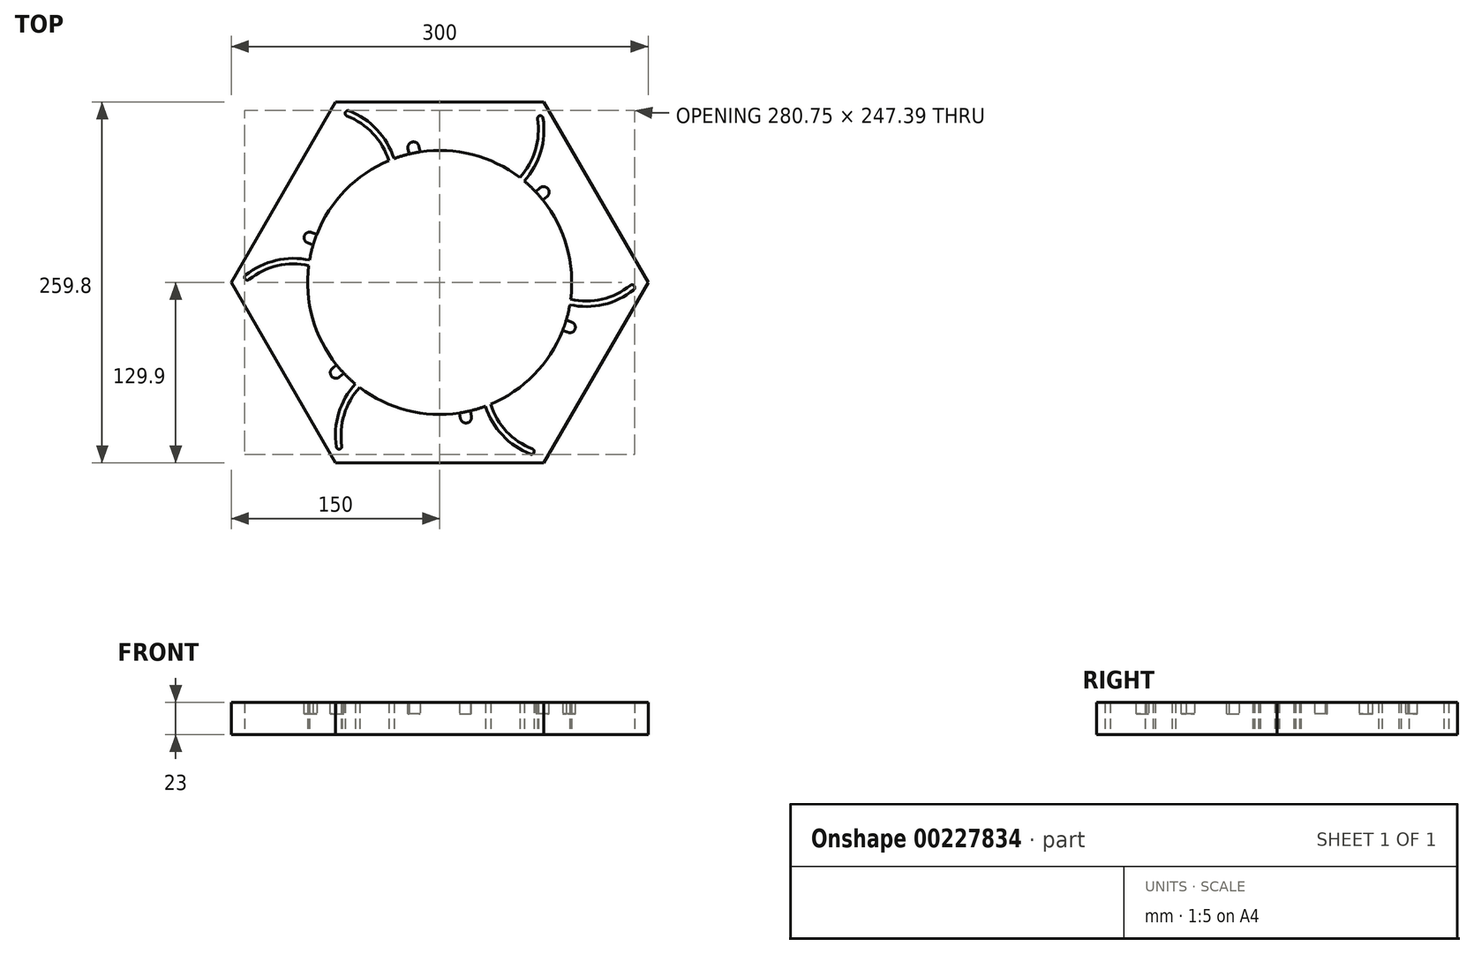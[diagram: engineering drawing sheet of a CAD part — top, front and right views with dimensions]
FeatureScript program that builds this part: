
annotation { "Feature Type Name" : "Feature", "Feature Type Description" : "" }
export const myFeature = defineFeature(function(context is Context, id is Id, definition is map)
    precondition{}
    {
        {
            var Q0;
            Q0=qCreatedBy(makeId("Top.planeOp"),FACE);
            var sketch = newSketch(context, id + "F0", { "sketchPlane" : qUnion([Q0])});
            skCircle(sketch, "E0.cCircle", {"center": v(0, 0) * mm, "radius": 150 * mm, "construction": true});
            skLineSegment(sketch, "E0.0", {"start": v(-75, 129.9) * mm, "end": v(75, 129.9) * mm});
            skLineSegment(sketch, "E0.1", {"start": v(75, 129.9) * mm, "end": v(150, 0) * mm});
            skLineSegment(sketch, "E0.2", {"start": v(150, 0) * mm, "end": v(75, -129.9) * mm});
            skLineSegment(sketch, "E0.3", {"start": v(75, -129.9) * mm, "end": v(-75, -129.9) * mm});
            skLineSegment(sketch, "E0.4", {"start": v(-75, -129.9) * mm, "end": v(-150, 0) * mm});
            skLineSegment(sketch, "E0.5", {"start": v(-150, 0) * mm, "end": v(-75, 129.9) * mm});
            skCircle(sketch, "E1", {"center": v(0, 0) * mm, "radius": 95 * mm});
            skSolve(sketch);
        }
        {
            var Q0;
            Q0=qCreatedBy(makeId("Front.planeOp"),FACE);
            var sketch = newSketch(context, id + "F1", { "sketchPlane" : qUnion([Q0])});
            skLineSegment(sketch, "E2", {"start": v(0, -93.36) * mm, "end": v(0, 93) * mm, "construction": true});
            skSolve(sketch);
        }
        {
            var Q0;
            Q0=makeQuery(id+"F0.imprint","IMPRINT",FACE,{"disambiguationData":[TD([[makeQuery(id+"F0.imprint","IMPRINT",EDGE,{"derivedFrom":sQuery(id+"F0.wireOp",EDGE,"E0.0")}),-1.0]])]});
            extrude(context, id + "F2", {"entities" : qUnion([Q0]), "depth" : 25 * mm, "hasSecondDirection" : true, "secondDirectionOppositeDirection" : false, "secondDirectionDepth" : 2 * mm});
        }
        {
            var Q0;
            Q0=qCreatedBy(makeId("Top.planeOp"),FACE);
            var sketch = newSketch(context, id + "F3", { "sketchPlane" : qUnion([Q0])});
            skArc(sketch, "E3.0", {"start": v(-30.7, 79.26) * mm, "mid": v(-41.9, 106.16) * mm, "end": v(-65.27, 123.56) * mm});
            skArc(sketch, "E4.0", {"start": v(-34.54, 77.66) * mm, "mid": v(-44.72, 103.26) * mm, "end": v(-66.72, 119.83) * mm});
            skArc(sketch, "E5.0", {"start": v(-67.73, 122.7) * mm, "mid": v(-67.88, 121.03) * mm, "end": v(-66.72, 119.83) * mm});
            skArc(sketch, "E6.0", {"start": v(-65.27, 123.56) * mm, "mid": v(-66.66, 123.58) * mm, "end": v(-67.73, 122.7) * mm});
            skArc(sketch, "E7.0", {"start": v(-30.7, 79.26) * mm, "mid": v(-32.63, 78.49) * mm, "end": v(-34.54, 77.66) * mm});
            skSolve(sketch);
        }
        {
            var Q0;
            Q0 = qSketchRegion(id + "F3", true);
            extrude(context, id + "F4", {"entities" : qUnion([Q0]), "depth" : 35 * mm, "hasSecondDirection" : true, "secondDirectionOppositeDirection" : true, "secondDirectionDepth" : 10 * mm});
        }
        {
            var Q0;
            Q0=makeQuery(id+"F4.opExtrude","SWEPT_BODY",BODY,{"disambiguationData":[OSD([sQuery(id+"F3.wireOp",EDGE,"E3.0"),sQuery(id+"F3.wireOp",EDGE,"E4.0"),sQuery(id+"F3.wireOp",EDGE,"E5.0"),sQuery(id+"F3.wireOp",EDGE,"E6.0"),sQuery(id+"F3.wireOp",EDGE,"E7.0")])]});
            var Q1;
            Q1=sQuery(id+"F1.wireOp",EDGE,"E2");
            circularPattern(context, id + "F5", {"entities" : qUnion([Q0]), "axis" : qUnion([Q1]), "angle" : 360 * degree, "instanceCount" : 6, "equalSpace" : true});
        }
        {
            var Q0;
            Q0=makeQuery(id+"F4.opExtrude","SWEPT_BODY",BODY,{"disambiguationData":[OSD([sQuery(id+"F3.wireOp",EDGE,"E3.0"),sQuery(id+"F3.wireOp",EDGE,"E4.0"),sQuery(id+"F3.wireOp",EDGE,"E5.0"),sQuery(id+"F3.wireOp",EDGE,"E6.0"),sQuery(id+"F3.wireOp",EDGE,"E7.0")])]});
            var Q1;
            Q1=makeQuery(id+"F5.opPattern","COPY",BODY,{"derivedFrom":makeQuery(id+"F4.opExtrude","SWEPT_BODY",BODY,{"disambiguationData":[OSD([sQuery(id+"F3.wireOp",EDGE,"E3.0"),sQuery(id+"F3.wireOp",EDGE,"E4.0"),sQuery(id+"F3.wireOp",EDGE,"E5.0"),sQuery(id+"F3.wireOp",EDGE,"E6.0"),sQuery(id+"F3.wireOp",EDGE,"E7.0")])]}),"instanceName":"5"});
            var Q2;
            Q2=makeQuery(id+"F5.opPattern","COPY",BODY,{"derivedFrom":makeQuery(id+"F4.opExtrude","SWEPT_BODY",BODY,{"disambiguationData":[OSD([sQuery(id+"F3.wireOp",EDGE,"E3.0"),sQuery(id+"F3.wireOp",EDGE,"E4.0"),sQuery(id+"F3.wireOp",EDGE,"E5.0"),sQuery(id+"F3.wireOp",EDGE,"E6.0"),sQuery(id+"F3.wireOp",EDGE,"E7.0")])]}),"instanceName":"4"});
            var Q3;
            Q3=makeQuery(id+"F5.opPattern","COPY",BODY,{"derivedFrom":makeQuery(id+"F4.opExtrude","SWEPT_BODY",BODY,{"disambiguationData":[OSD([sQuery(id+"F3.wireOp",EDGE,"E3.0"),sQuery(id+"F3.wireOp",EDGE,"E4.0"),sQuery(id+"F3.wireOp",EDGE,"E5.0"),sQuery(id+"F3.wireOp",EDGE,"E6.0"),sQuery(id+"F3.wireOp",EDGE,"E7.0")])]}),"instanceName":"3"});
            var Q4;
            Q4=makeQuery(id+"F5.opPattern","COPY",BODY,{"derivedFrom":makeQuery(id+"F4.opExtrude","SWEPT_BODY",BODY,{"disambiguationData":[OSD([sQuery(id+"F3.wireOp",EDGE,"E3.0"),sQuery(id+"F3.wireOp",EDGE,"E4.0"),sQuery(id+"F3.wireOp",EDGE,"E5.0"),sQuery(id+"F3.wireOp",EDGE,"E6.0"),sQuery(id+"F3.wireOp",EDGE,"E7.0")])]}),"instanceName":"2"});
            var Q5;
            Q5=makeQuery(id+"F5.opPattern","COPY",BODY,{"derivedFrom":makeQuery(id+"F4.opExtrude","SWEPT_BODY",BODY,{"disambiguationData":[OSD([sQuery(id+"F3.wireOp",EDGE,"E3.0"),sQuery(id+"F3.wireOp",EDGE,"E4.0"),sQuery(id+"F3.wireOp",EDGE,"E5.0"),sQuery(id+"F3.wireOp",EDGE,"E6.0"),sQuery(id+"F3.wireOp",EDGE,"E7.0")])]}),"instanceName":"1"});
            var Q6;
            Q6=makeQuery(id+"F2.opExtrude","SWEPT_BODY",BODY,{"disambiguationData":[OSD([sQuery(id+"F0.wireOp",EDGE,"E0.0"),sQuery(id+"F0.wireOp",EDGE,"E0.1"),sQuery(id+"F0.wireOp",EDGE,"E0.2"),sQuery(id+"F0.wireOp",EDGE,"E0.3"),sQuery(id+"F0.wireOp",EDGE,"E0.4"),sQuery(id+"F0.wireOp",EDGE,"E0.5"),sQuery(id+"F0.wireOp",EDGE,"E1")])]});
            booleanBodies(context, id + "F6", {"operationType" : BooleanOperationType.SUBTRACTION, "tools" : qUnion([Q0, Q1, Q2, Q3, Q4, Q5]), "targets" : qUnion([Q6])});
        }
        {
            var Q0;
            Q0=makeQuery(id+"F2.opExtrude","CAP_FACE",FACE,{"disambiguationData":[OSD([sQuery(id+"F0.wireOp",EDGE,"E0.0"),sQuery(id+"F0.wireOp",EDGE,"E0.1"),sQuery(id+"F0.wireOp",EDGE,"E0.2"),sQuery(id+"F0.wireOp",EDGE,"E0.3"),sQuery(id+"F0.wireOp",EDGE,"E0.4"),sQuery(id+"F0.wireOp",EDGE,"E0.5"),sQuery(id+"F0.wireOp",EDGE,"E1")])],"isStart":false});
            var sketch = newSketch(context, id + "F7", { "sketchPlane" : qUnion([Q0])});
            skCircle(sketch, "E8", {"center": v(0, 0) * mm, "radius": 95 * mm, "construction": true});
            skCircle(sketch, "E9", {"center": v(0, 0) * mm, "radius": 99 * mm, "construction": true});
            skLineSegment(sketch, "E10", {"start": v(0, 0) * mm, "end": v(0, 115.62) * mm, "construction": true});
            skLineSegment(sketch, "E11", {"start": v(0, 0) * mm, "end": v(-23.06, 118.63) * mm, "construction": true});
            skPoint(sketch, "E12", {"position": v(-18.9, 97.18) * mm});
            skArc(sketch, "E13", {"start": v(-19.65, 101.1) * mm, "mid": v(-22.23, 99.38) * mm, "end": v(-22.8, 96.34) * mm});
            skLineSegment(sketch, "E14", {"start": v(-22.82, 96.42) * mm, "end": v(-20.7, 85.51) * mm});
            skLineSegment(sketch, "E15", {"start": v(-16.77, 86.28) * mm, "end": v(-20.7, 85.51) * mm});
            skArc(sketch, "E16.MirrorCS", {"start": v(-19.65, 101.1) * mm, "mid": v(-16.62, 100.47) * mm, "end": v(-14.95, 97.86) * mm});
            skLineSegment(sketch, "E17.MirrorCS", {"start": v(-16.77, 86.28) * mm, "end": v(-12.84, 87.04) * mm});
            skLineSegment(sketch, "E18.MirrorCS", {"start": v(-14.96, 97.94) * mm, "end": v(-12.84, 87.04) * mm});
            skSolve(sketch);
        }
        {
            var Q0;
            Q0 = qSketchRegion(id + "F7", true);
            extrude(context, id + "F8", {"entities" : qUnion([Q0]), "oppositeDirection" : true, "depth" : 8 * mm, "hasSecondDirection" : true, "secondDirectionOppositeDirection" : false, "secondDirectionDepth" : 10 * mm});
        }
        {
            var Q0;
            Q0=makeQuery(id+"F8.opExtrude","SWEPT_BODY",BODY,{"disambiguationData":[OSD([sQuery(id+"F7.wireOp",EDGE,"E13"),sQuery(id+"F7.wireOp",EDGE,"E14"),sQuery(id+"F7.wireOp",EDGE,"E15"),sQuery(id+"F7.wireOp",EDGE,"E16.MirrorCS"),sQuery(id+"F7.wireOp",EDGE,"E17.MirrorCS"),sQuery(id+"F7.wireOp",EDGE,"E18.MirrorCS")])]});
            var Q1;
            Q1=sQuery(id+"F1.wireOp",EDGE,"E2");
            circularPattern(context, id + "F9", {"operationType" : NewBodyOperationType.REMOVE, "entities" : qUnion([Q0]), "axis" : qUnion([Q1]), "angle" : 360 * degree, "instanceCount" : 6, "equalSpace" : true});
        }
    });
